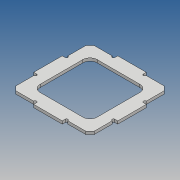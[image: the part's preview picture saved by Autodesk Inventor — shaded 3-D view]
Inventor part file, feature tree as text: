
AUTODESK INVENTOR PART (.ipt)
format: ipt  version: 2017 (Build 210142000, 142)  size: 136,704 bytes
history: native  units: mm
features: other x1, extrude x1, sketch x1
ambient origin geometry x8: Origin, YZ Plane, XZ Plane, XY Plane, X Axis, Y Axis, Z Axis, Center Point
bodies: Body1 (feature_tree)
feature tree (3):
  other  "Sólido1"
  extrude  "Extrusión1"  Depth=40.0mm
  sketch  "Boceto1"  dims[d0=110.0mm d1=40.0mm d2=2.0mm d3=110.0mm d7=4.0mm d8=6.0mm d9=6.0mm d10=6.0mm d11=6.0mm d12=6.0mm d13=6.0mm d14=6.0mm d15=6.0mm d16=15.0mm d17=10.0mm d18=4.0mm d19=0.0mm]
